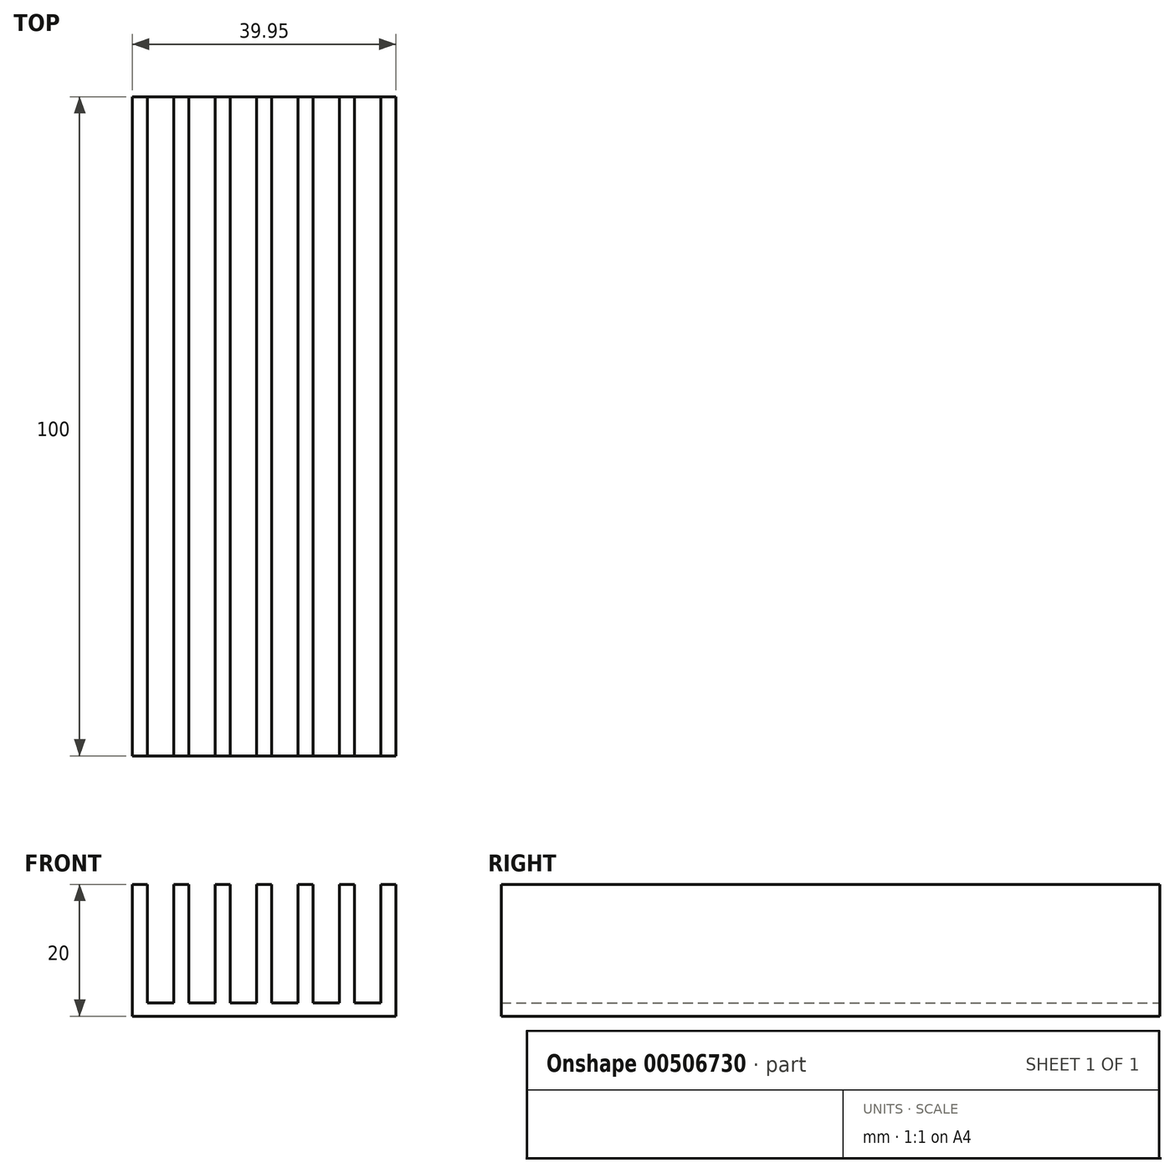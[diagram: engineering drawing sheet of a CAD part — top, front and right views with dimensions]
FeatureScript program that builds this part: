
annotation { "Feature Type Name" : "Feature", "Feature Type Description" : "" }
export const myFeature = defineFeature(function(context is Context, id is Id, definition is map)
    precondition{}
    {
        {
            var Q0;
            Q0=qCreatedBy(makeId("Front.planeOp"),FACE);
            var sketch = newSketch(context, id + "F0", { "sketchPlane" : qUnion([Q0])});
            skLineSegment(sketch, "E0.bottom", {"start": v(20, 10) * mm, "end": v(17.69, 10) * mm});
            skLineSegment(sketch, "E0.top", {"start": v(20, -10) * mm, "end": v(-20, -10) * mm});
            skLineSegment(sketch, "E0.left", {"start": v(20, 10) * mm, "end": v(20, -10) * mm});
            skLineSegment(sketch, "E0.right", {"start": v(-20, 10) * mm, "end": v(-20, -10) * mm});
            skPoint(sketch, "E0.middle", {"position": v(0, 0) * mm});
            skLineSegment(sketch, "E1.0", {"start": v(-17.71, 10) * mm, "end": v(-17.71, -8) * mm});
            skLineSegment(sketch, "E2.0", {"start": v(20, -8) * mm, "end": v(19.95, -8) * mm});
            skLineSegment(sketch, "E3.0", {"start": v(-13.71, 10) * mm, "end": v(-13.71, -8) * mm});
            skLineSegment(sketch, "E4.0", {"start": v(-11.43, 10) * mm, "end": v(-11.43, -8) * mm});
            skLineSegment(sketch, "E5.0", {"start": v(-7.43, 10) * mm, "end": v(-7.43, -8) * mm});
            skLineSegment(sketch, "E6.0", {"start": v(-5.14, 10) * mm, "end": v(-5.14, -8) * mm});
            skLineSegment(sketch, "E7.0", {"start": v(-1.14, 10) * mm, "end": v(-1.14, -8) * mm});
            skLineSegment(sketch, "E8.0", {"start": v(1.14, 10) * mm, "end": v(1.14, -8) * mm});
            skLineSegment(sketch, "E9.0", {"start": v(5.14, 10) * mm, "end": v(5.14, -8) * mm});
            skLineSegment(sketch, "E10.0", {"start": v(7.43, 10) * mm, "end": v(7.43, -8) * mm});
            skLineSegment(sketch, "E11.0", {"start": v(11.43, 10) * mm, "end": v(11.43, -8) * mm});
            skLineSegment(sketch, "E12.0", {"start": v(13.69, 10) * mm, "end": v(13.69, -8) * mm});
            skLineSegment(sketch, "E13.0", {"start": v(17.69, 10) * mm, "end": v(17.69, -8) * mm});
            skLineSegment(sketch, "E14.0", {"start": v(19.95, 10) * mm, "end": v(19.95, -10) * mm});
            skLineSegment(sketch, "E15.trimOffspring", {"start": v(-13.71, -8) * mm, "end": v(-17.71, -8) * mm});
            skLineSegment(sketch, "E16.trimOffspring", {"start": v(-7.43, -8) * mm, "end": v(-11.43, -8) * mm});
            skLineSegment(sketch, "E17.trimOffspring", {"start": v(-1.14, -8) * mm, "end": v(-5.14, -8) * mm});
            skLineSegment(sketch, "E18.trimOffspring", {"start": v(5.14, -8) * mm, "end": v(1.14, -8) * mm});
            skLineSegment(sketch, "E19.trimOffspring", {"start": v(11.43, -8) * mm, "end": v(7.43, -8) * mm});
            skLineSegment(sketch, "E20.trimOffspring", {"start": v(17.69, -8) * mm, "end": v(13.69, -8) * mm});
            skLineSegment(sketch, "E21.trimOffspring", {"start": v(-17.71, 10) * mm, "end": v(-20, 10) * mm});
            skLineSegment(sketch, "E22.trimOffspring", {"start": v(-11.43, 10) * mm, "end": v(-13.71, 10) * mm});
            skLineSegment(sketch, "E23.trimOffspring", {"start": v(-5.14, 10) * mm, "end": v(-7.43, 10) * mm});
            skLineSegment(sketch, "E24.trimOffspring", {"start": v(1.14, 10) * mm, "end": v(-1.14, 10) * mm});
            skLineSegment(sketch, "E25.trimOffspring", {"start": v(7.43, 10) * mm, "end": v(5.14, 10) * mm});
            skLineSegment(sketch, "E26.trimOffspring", {"start": v(13.69, 10) * mm, "end": v(11.43, 10) * mm});
            skSolve(sketch);
        }
        {
            var Q0;
            {var subQ7=sQuery(id+"F0.wireOp",EDGE,"E0.right");Q0=makeQuery(id+"F0.imprint","IMPRINT",FACE,{"disambiguationData":[TD([[makeQuery(id+"F0.imprint","IMPRINT",EDGE,{"derivedFrom":subQ7}),1.0]])]});}
            extrude(context, id + "F1", {"entities" : qUnion([Q0]), "endBound" : BoundingType.SYMMETRIC, "depth" : 100 * mm, "offsetDistance" : 25 * mm});
        }
    });
